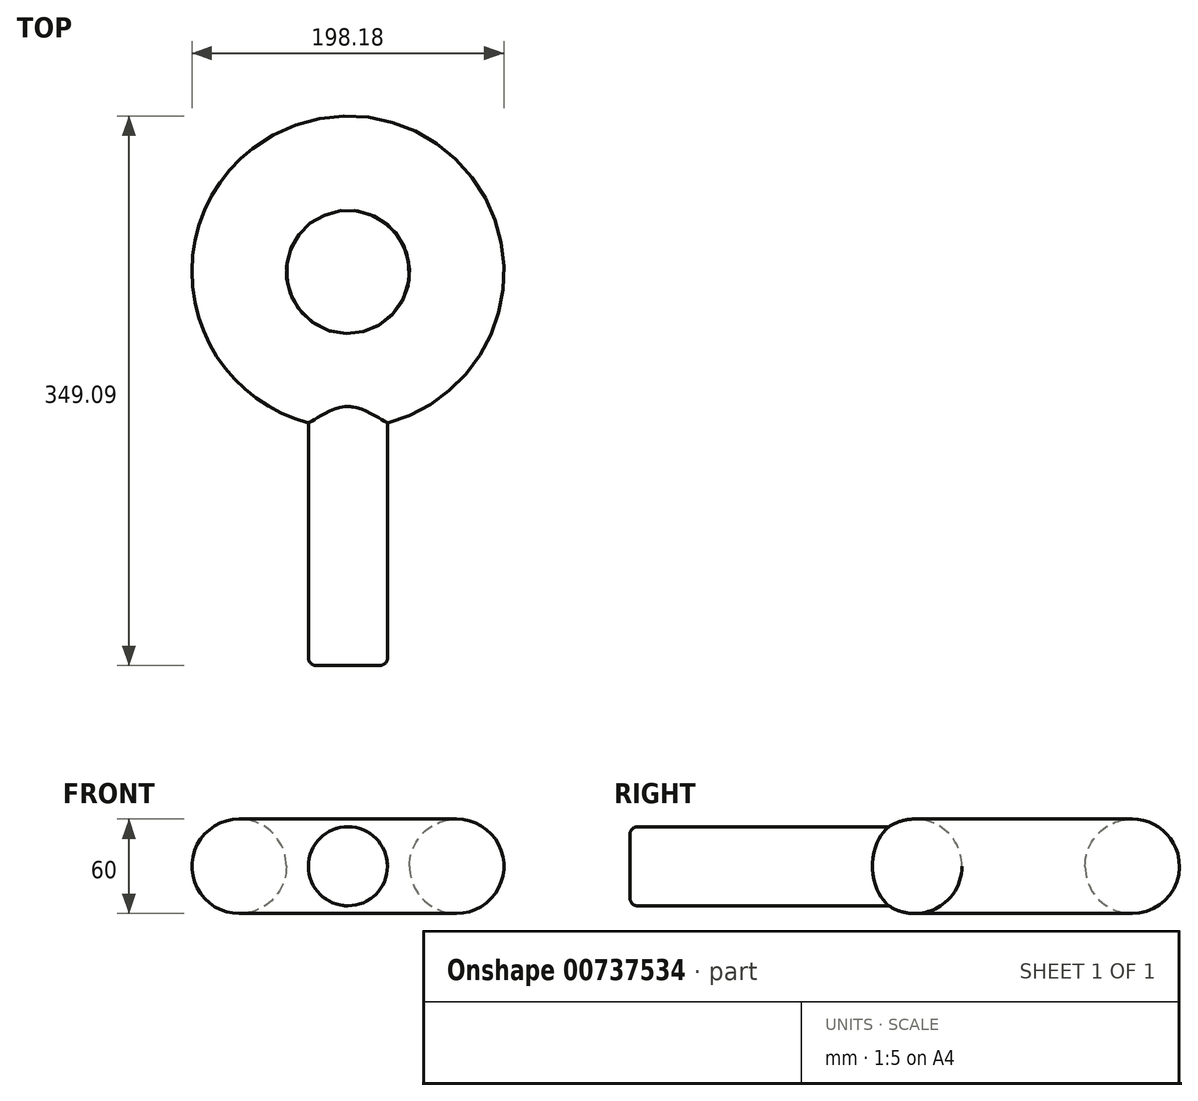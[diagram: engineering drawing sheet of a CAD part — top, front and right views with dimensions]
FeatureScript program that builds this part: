
annotation { "Feature Type Name" : "Feature", "Feature Type Description" : "" }
export const myFeature = defineFeature(function(context is Context, id is Id, definition is map)
    precondition{}
    {
        {
            var Q0;
            Q0=qCreatedBy(makeId("Front.planeOp"),FACE);
            var sketch = newSketch(context, id + "F0", { "sketchPlane" : qUnion([Q0])});
            skCircle(sketch, "E0", {"center": v(-69.09, 0) * mm, "radius": 30 * mm});
            skSolve(sketch);
        }
        {
            var Q0;
            Q0=qCreatedBy(makeId("Front.planeOp"),FACE);
            var sketch = newSketch(context, id + "F1", { "sketchPlane" : qUnion([Q0])});
            skLineSegment(sketch, "E1", {"start": v(0, 51.84) * mm, "end": v(0, -41.81) * mm});
            skSolve(sketch);
        }
        {
            var Q0;
            Q0=makeQuery(id+"F0.imprint","IMPRINT",FACE,{"disambiguationData":[TD([[makeQuery(id+"F0.imprint","IMPRINT",EDGE,{"derivedFrom":sQuery(id+"F0.wireOp",EDGE,"E0")}),1.0]])]});
            var Q1;
            Q1=sQuery(id+"F1.wireOp",EDGE,"E1");
            revolve(context, id + "F2", {"surfaceOperationType" : NewSurfaceOperationType.NEW, "entities" : qUnion([Q0]), "axis" : qUnion([Q1]), "revolveType" : RevolveType.FULL});
        }
        {
            var Q0;
            Q0=qCreatedBy(makeId("Front.planeOp"),FACE);
            cPlane(context, id + "F3", {"entities" : qUnion([Q0]), "cplaneType" : CPlaneType.OFFSET, "offset" : 100 * mm, "width" : 150 * mm, "height" : 150 * mm});
        }
        {
            var Q0;
            Q0=qCreatedBy(id+"F3.planeOp",FACE);
            var sketch = newSketch(context, id + "F4", { "sketchPlane" : qUnion([Q0])});
            skCircle(sketch, "E2", {"center": v(0, 0) * mm, "radius": 25.12 * mm});
            skSolve(sketch);
        }
        {
            var Q0;
            Q0=makeQuery(id+"F4.imprint","IMPRINT",FACE,{"disambiguationData":[TD([[makeQuery(id+"F4.imprint","IMPRINT",EDGE,{"derivedFrom":sQuery(id+"F4.wireOp",EDGE,"E2")}),1.0]])]});
            var Q1;
            Q1=sQuery(id+"F4.wireOp",EDGE,"E2");
            extrude(context, id + "F5", {"entities" : qUnion([Q0]), "operationType" : NewBodyOperationType.ADD, "surfaceEntities" : qUnion([Q1]), "endBound" : BoundingType.UP_TO_NEXT, "oppositeDirection" : true, "depth" : 25 * mm, "offsetDistance" : 25 * mm});
        }
        {
            var Q0;
            Q0=makeQuery(id+"F5.opExtrude","CAP_FACE",FACE,{"disambiguationData":[OSD([sQuery(id+"F4.wireOp",EDGE,"E2")])],"isStart":true});
            extrude(context, id + "F6", {"entities" : qUnion([Q0]), "operationType" : NewBodyOperationType.ADD, "depth" : 150 * mm, "offsetDistance" : 25 * mm});
        }
        {
            var Q0;
            Q0=makeQuery(id+"F6.opExtrude","CAP_EDGE",EDGE,{"disambiguationData":[OSD([sQuery(id+"F4.wireOp",EDGE,"E2")])],"isStart":false});
            var Q1;
            Q1=makeQuery(id+"F5.opExtrude","CAP_EDGE",EDGE,{"disambiguationData":[OSD([sQuery(id+"F4.wireOp",EDGE,"E2")])],"isStart":false});
            fillet(context, id + "F7", {"entities" : qUnion([Q0, Q1]), "radius" : 5 * mm, "tangentPropagation" : true, "allowEdgeOverflow" : false});
        }
    });
